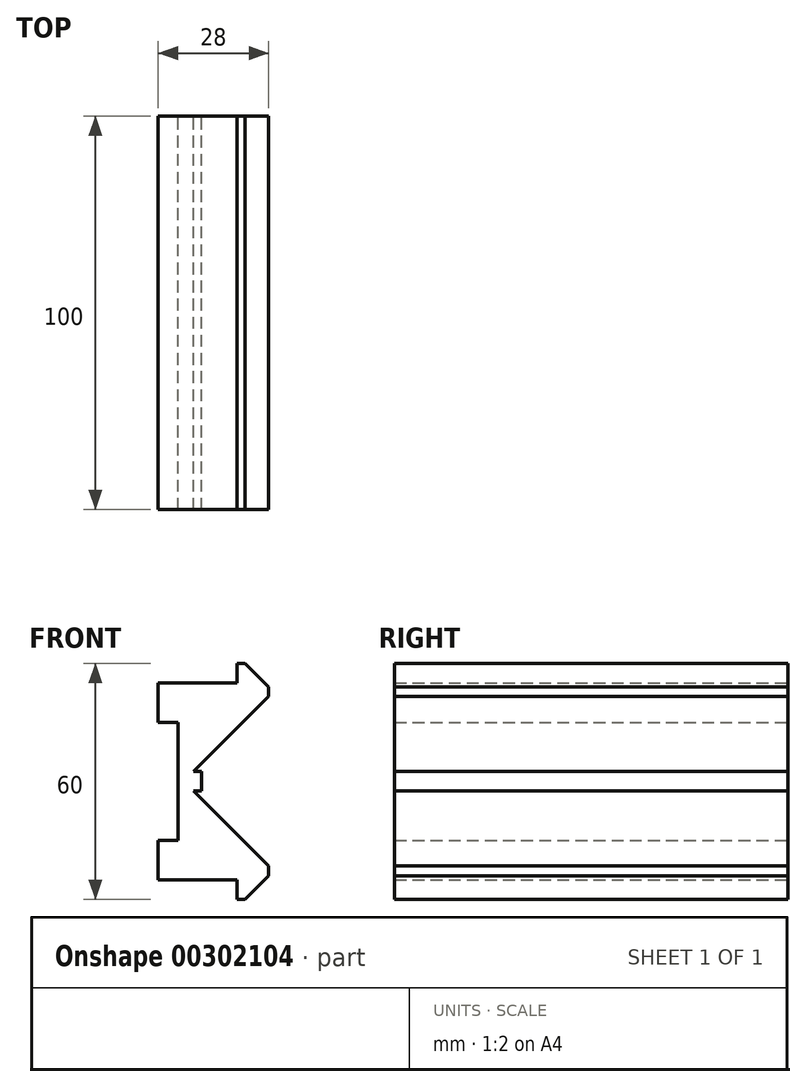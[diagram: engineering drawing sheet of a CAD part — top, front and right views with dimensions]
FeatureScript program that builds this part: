
annotation { "Feature Type Name" : "Feature", "Feature Type Description" : "" }
export const myFeature = defineFeature(function(context is Context, id is Id, definition is map)
    precondition{}
    {
        {
            var Q0;
            Q0=qCreatedBy(makeId("Front.planeOp"),FACE);
            var sketch = newSketch(context, id + "F0", { "sketchPlane" : qUnion([Q0])});
            skLineSegment(sketch, "E0", {"start": v(0, 0) * mm, "end": v(0, 15) * mm});
            skLineSegment(sketch, "E1", {"start": v(0, 15) * mm, "end": v(-5, 15) * mm});
            skLineSegment(sketch, "E2", {"start": v(-5, 15) * mm, "end": v(-5, 25) * mm});
            skLineSegment(sketch, "E3", {"start": v(-5, 25) * mm, "end": v(15, 25) * mm});
            skLineSegment(sketch, "E4", {"start": v(15, 25) * mm, "end": v(15, 30) * mm});
            skLineSegment(sketch, "E5", {"start": v(15, 30) * mm, "end": v(17, 30) * mm});
            skLineSegment(sketch, "E6", {"start": v(17, 30) * mm, "end": v(23, 24) * mm});
            skLineSegment(sketch, "E7", {"start": v(23, 24) * mm, "end": v(23, 21.5) * mm});
            skPoint(sketch, "E8.end.orphan", {"position": v(15, 0) * mm});
            skPoint(sketch, "E9.end.orphan", {"position": v(1.5, 0) * mm});
            skPoint(sketch, "E9.start.orphan", {"position": v(12.51, 2.5) * mm});
            skPoint(sketch, "E10.end.orphan", {"position": v(15, 2.5) * mm});
            skLineSegment(sketch, "E11", {"start": v(23, 21.5) * mm, "end": v(4, 2.5) * mm});
            skLineSegment(sketch, "E12", {"start": v(6, 2.5) * mm, "end": v(4, 2.5) * mm});
            skLineSegment(sketch, "E13", {"start": v(6, 2.5) * mm, "end": v(6, 0) * mm});
            skLineSegment(sketch, "E14.MirrorCS", {"start": v(6, -2.5) * mm, "end": v(6, 0) * mm});
            skLineSegment(sketch, "E15.MirrorCS", {"start": v(6, -2.5) * mm, "end": v(4, -2.5) * mm});
            skLineSegment(sketch, "E16.MirrorCS", {"start": v(23, -21.5) * mm, "end": v(4, -2.5) * mm});
            skLineSegment(sketch, "E17.MirrorCS", {"start": v(23, -24) * mm, "end": v(23, -21.5) * mm});
            skLineSegment(sketch, "E18.MirrorCS", {"start": v(17, -30) * mm, "end": v(23, -24) * mm});
            skLineSegment(sketch, "E19.MirrorCS", {"start": v(15, -30) * mm, "end": v(17, -30) * mm});
            skLineSegment(sketch, "E20.MirrorCS", {"start": v(15, -25) * mm, "end": v(15, -30) * mm});
            skLineSegment(sketch, "E21.MirrorCS", {"start": v(-5, -25) * mm, "end": v(15, -25) * mm});
            skLineSegment(sketch, "E22.MirrorCS", {"start": v(-5, -15) * mm, "end": v(-5, -25) * mm});
            skLineSegment(sketch, "E23.MirrorCS", {"start": v(0, -15) * mm, "end": v(-5, -15) * mm});
            skLineSegment(sketch, "E24.MirrorCS", {"start": v(0, 0) * mm, "end": v(0, -15) * mm});
            skSolve(sketch);
        }
        {
            var Q0;
            Q0 = qSketchRegion(id + "F0", true);
            extrude(context, id + "F1", {"entities" : qUnion([Q0]), "depth" : 100 * mm});
        }
    });
